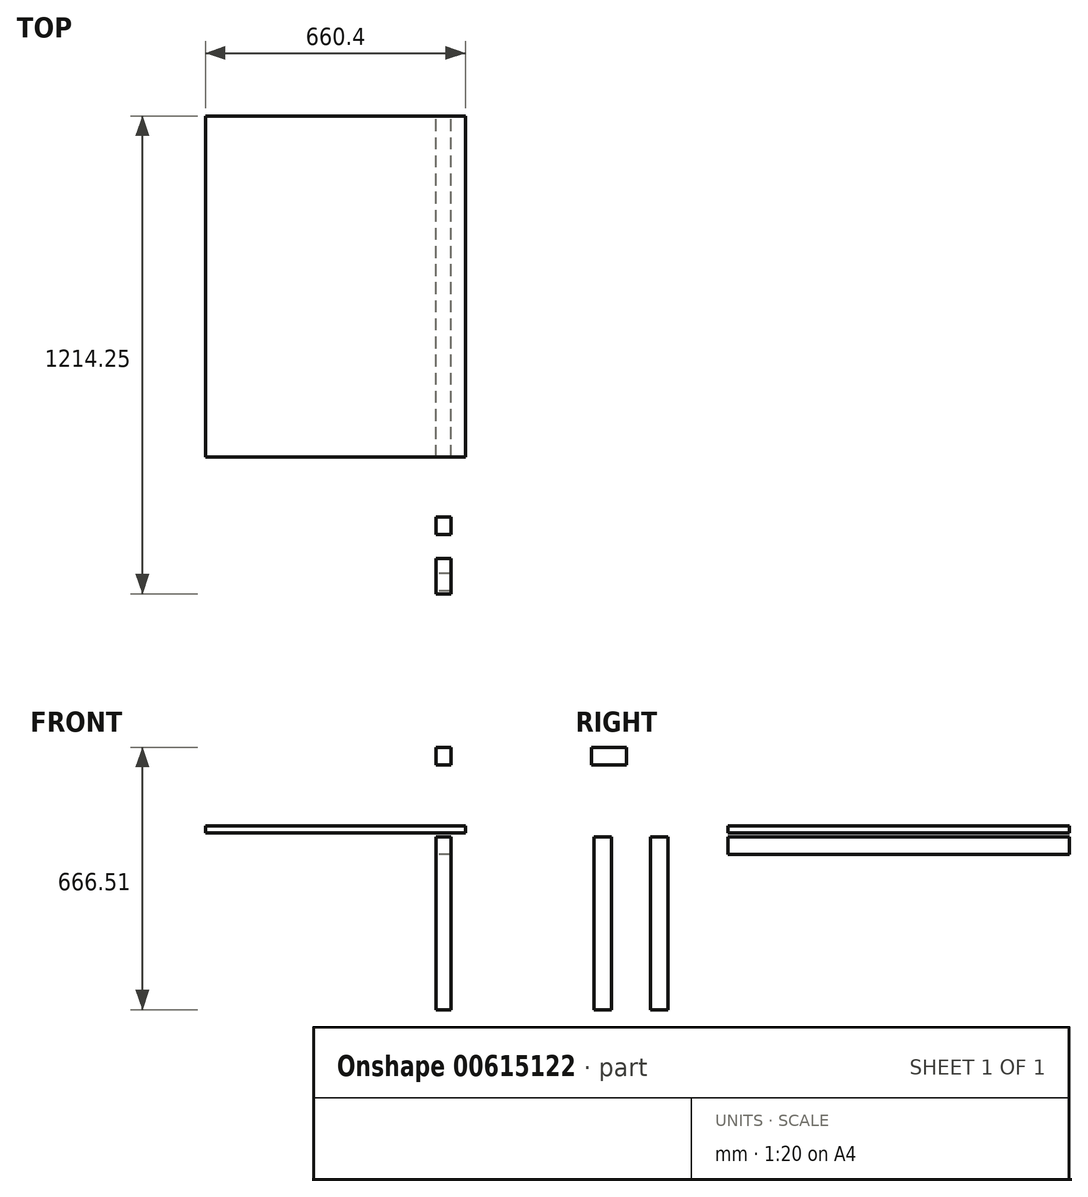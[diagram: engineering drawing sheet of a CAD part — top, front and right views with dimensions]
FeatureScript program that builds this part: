
annotation { "Feature Type Name" : "Feature", "Feature Type Description" : "" }
export const myFeature = defineFeature(function(context is Context, id is Id, definition is map)
    precondition{}
    {
        {
            var Q0;
            Q0=qCreatedBy(makeId("Front.planeOp"),FACE);
            var sketch = newSketch(context, id + "F0", { "sketchPlane" : qUnion([Q0])});
            skLineSegment(sketch, "E0.bottom", {"start": v(-586.04, 27.92) * mm, "end": v(74.36, 27.92) * mm});
            skLineSegment(sketch, "E0.top", {"start": v(-586.04, 10.14) * mm, "end": v(74.36, 10.14) * mm});
            skLineSegment(sketch, "E0.left", {"start": v(-586.04, 27.92) * mm, "end": v(-586.04, 10.14) * mm});
            skLineSegment(sketch, "E0.right", {"start": v(74.36, 27.92) * mm, "end": v(74.36, 10.14) * mm});
            skLineSegment(sketch, "E1.bottom", {"start": v(-586.06, 10.34) * mm, "end": v(74.34, 10.34) * mm});
            skLineSegment(sketch, "E1.top", {"start": v(-586.06, -3.88) * mm, "end": v(74.34, -3.88) * mm});
            skLineSegment(sketch, "E1.left", {"start": v(-586.06, 10.34) * mm, "end": v(-586.06, -3.88) * mm});
            skLineSegment(sketch, "E1.right", {"start": v(74.34, 10.34) * mm, "end": v(74.34, -3.88) * mm});
            skSolve(sketch);
        }
        {
            var Q0;
            {var subQ2=sQuery(id+"F0.wireOp",EDGE,"E0.bottom");Q0=makeQuery(id+"F0.imprint","IMPRINT",FACE,{"disambiguationData":[TD([[makeQuery(id+"F0.imprint","IMPRINT",EDGE,{"derivedFrom":subQ2}),-1.0]])]});}
            var Q1;
            {var subQ0=sQuery(id+"F0.wireOp",EDGE,"E1.top");Q1=makeQuery(id+"F0.imprint","IMPRINT",FACE,{"disambiguationData":[TD([[makeQuery(id+"F0.imprint","IMPRINT",EDGE,{"derivedFrom":subQ0}),1.0]])]});}
            extrude(context, id + "F1", {"entities" : qUnion([Q0, Q1]), "depth" : 866.65 * mm});
        }
        {
            var Q0;
            Q0=makeQuery(id+"F1.opExtrude","SWEPT_BODY",BODY,{"disambiguationData":[OSD([sQuery(id+"F0.wireOp",EDGE,"E0.top"),sQuery(id+"F0.wireOp",EDGE,"E0.left"),sQuery(id+"F0.wireOp",EDGE,"E1.bottom"),sQuery(id+"F0.wireOp",EDGE,"E1.top"),sQuery(id+"F0.wireOp",EDGE,"E1.left"),sQuery(id+"F0.wireOp",EDGE,"E1.right")])]});
            deleteBodies(context, id + "F2", {"entities" : qUnion([Q0])});
        }
        {
            var Q0;
            Q0=qCreatedBy(makeId("Right.planeOp"),FACE);
            var sketch = newSketch(context, id + "F3", { "sketchPlane" : qUnion([Q0])});
            skLineSegment(sketch, "E2.bottom", {"start": v(-866.65, 0) * mm, "end": v(0, 0) * mm});
            skLineSegment(sketch, "E2.top", {"start": v(-866.65, -44.45) * mm, "end": v(0, -44.45) * mm});
            skLineSegment(sketch, "E2.left", {"start": v(-866.65, 0) * mm, "end": v(-866.65, -44.45) * mm});
            skLineSegment(sketch, "E2.right", {"start": v(0, 0) * mm, "end": v(0, -44.45) * mm});
            skSolve(sketch);
        }
        {
            var Q0;
            Q0=makeQuery(id+"F3.imprint","IMPRINT",FACE,{"disambiguationData":[TD([[makeQuery(id+"F3.imprint","IMPRINT",EDGE,{"derivedFrom":sQuery(id+"F3.wireOp",EDGE,"E2.bottom")}),-1.0]])]});
            extrude(context, id + "F4", {"entities" : qUnion([Q0]), "depth" : 38.1 * mm});
        }
        {
            var Q0;
            Q0=qCreatedBy(makeId("Right.planeOp"),FACE);
            var sketch = newSketch(context, id + "F5", { "sketchPlane" : qUnion([Q0])});
            skLineSegment(sketch, "E3.bottom", {"start": v(-1063.56, 0) * mm, "end": v(-1019.11, 0) * mm});
            skLineSegment(sketch, "E3.top", {"start": v(-1063.56, -438.91) * mm, "end": v(-1019.11, -438.91) * mm});
            skLineSegment(sketch, "E3.left", {"start": v(-1063.56, 0) * mm, "end": v(-1063.56, -438.91) * mm});
            skLineSegment(sketch, "E3.right", {"start": v(-1019.11, 0) * mm, "end": v(-1019.11, -438.91) * mm});
            skSolve(sketch);
        }
        {
            var Q0;
            Q0=qCreatedBy(makeId("Right.planeOp"),FACE);
            var sketch = newSketch(context, id + "F6", { "sketchPlane" : qUnion([Q0])});
            skLineSegment(sketch, "E4.bottom", {"start": v(-1162.67, 0) * mm, "end": v(-1207.12, 0) * mm});
            skLineSegment(sketch, "E4.top", {"start": v(-1162.67, -438.91) * mm, "end": v(-1207.12, -438.91) * mm});
            skLineSegment(sketch, "E4.left", {"start": v(-1162.67, 0) * mm, "end": v(-1162.67, -438.91) * mm});
            skLineSegment(sketch, "E4.right", {"start": v(-1207.12, 0) * mm, "end": v(-1207.12, -438.91) * mm});
            skSolve(sketch);
        }
        {
            var Q0;
            Q0=qSketchRegion(id+"F6",true);
            extrude(context, id + "F7", {"entities" : qUnion([Q0]), "depth" : 38.1 * mm});
        }
        {
            var Q0;
            Q0=makeQuery(id+"F5.imprint","IMPRINT",FACE,{"disambiguationData":[TD([[makeQuery(id+"F5.imprint","IMPRINT",EDGE,{"derivedFrom":sQuery(id+"F5.wireOp",EDGE,"E3.bottom")}),-1.0]])]});
            extrude(context, id + "F8", {"entities" : qUnion([Q0]), "depth" : 38.1 * mm});
        }
        {
            var Q0;
            Q0=qCreatedBy(makeId("Right.planeOp"),FACE);
            var sketch = newSketch(context, id + "F9", { "sketchPlane" : qUnion([Q0])});
            skLineSegment(sketch, "E5.bottom", {"start": v(-1214.25, 227.6) * mm, "end": v(-1124.84, 227.6) * mm});
            skLineSegment(sketch, "E5.top", {"start": v(-1214.25, 183.15) * mm, "end": v(-1124.84, 183.15) * mm});
            skLineSegment(sketch, "E5.left", {"start": v(-1214.25, 227.6) * mm, "end": v(-1214.25, 183.15) * mm});
            skLineSegment(sketch, "E5.right", {"start": v(-1124.84, 227.6) * mm, "end": v(-1124.84, 183.15) * mm});
            skSolve(sketch);
        }
        {
            var Q0;
            Q0=makeQuery(id+"F9.imprint","IMPRINT",FACE,{"disambiguationData":[TD([[makeQuery(id+"F9.imprint","IMPRINT",EDGE,{"derivedFrom":sQuery(id+"F9.wireOp",EDGE,"E5.bottom")}),-1.0]])]});
            extrude(context, id + "F10", {"entities" : qUnion([Q0]), "depth" : 38.1 * mm});
        }
    });
